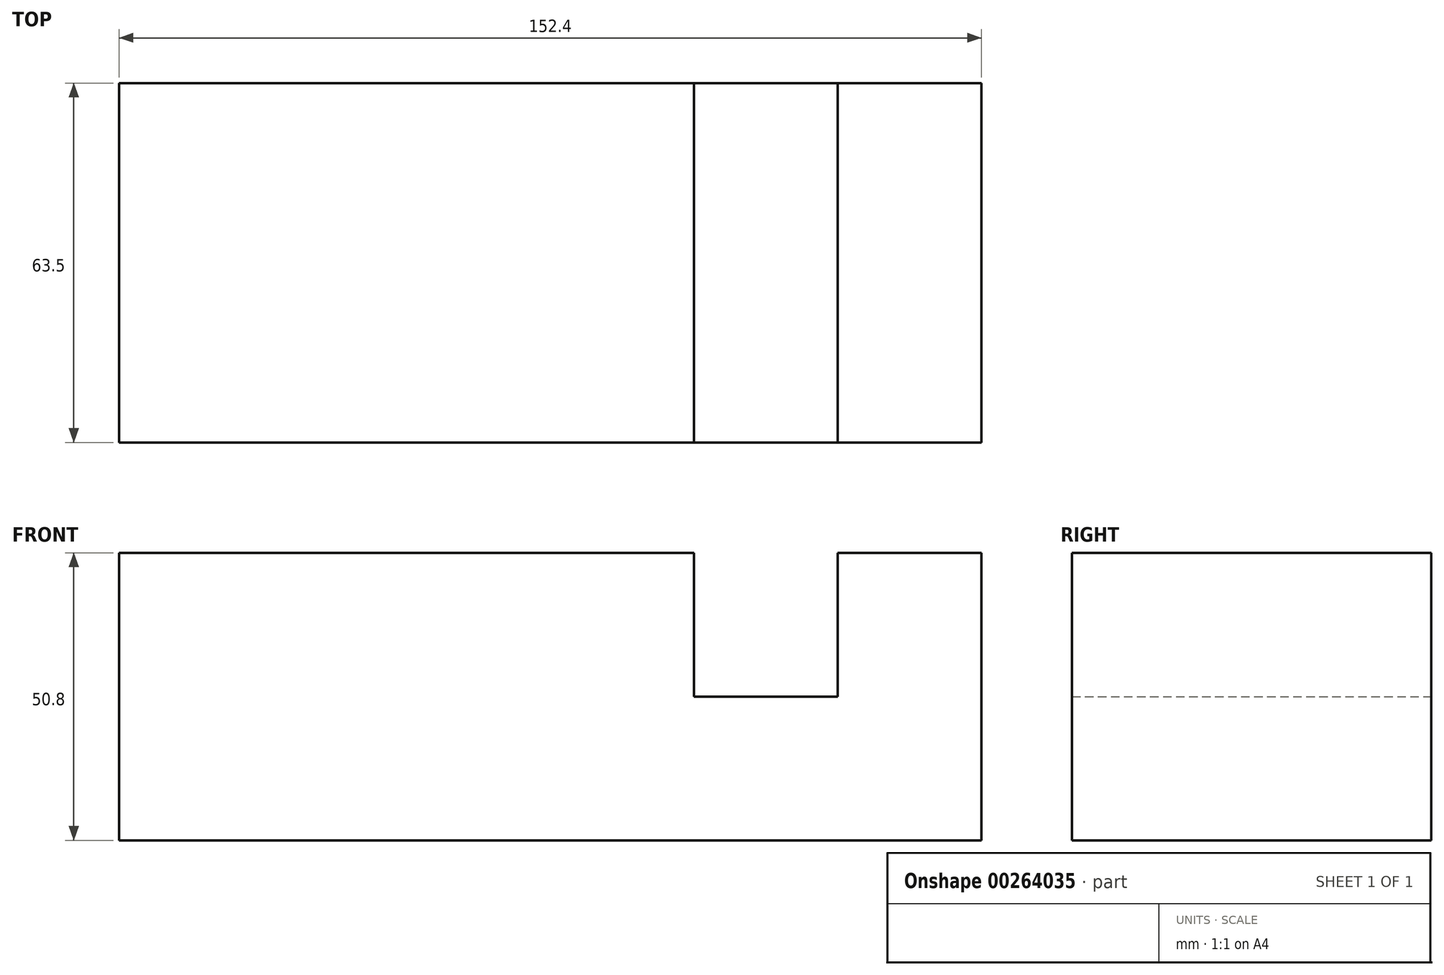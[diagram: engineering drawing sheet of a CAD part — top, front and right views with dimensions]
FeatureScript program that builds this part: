
annotation { "Feature Type Name" : "Feature", "Feature Type Description" : "" }
export const myFeature = defineFeature(function(context is Context, id is Id, definition is map)
    precondition{}
    {
        {
            var Q0;
            Q0=qCreatedBy(makeId("Front.planeOp"),FACE);
            var sketch = newSketch(context, id + "F0", { "sketchPlane" : qUnion([Q0])});
            skLineSegment(sketch, "E0", {"start": v(-75.34, -27.2) * mm, "end": v(77.06, -27.2) * mm});
            skLineSegment(sketch, "E1", {"start": v(77.06, -27.2) * mm, "end": v(77.06, 23.6) * mm});
            skLineSegment(sketch, "E2", {"start": v(77.06, 23.6) * mm, "end": v(51.66, 23.6) * mm});
            skLineSegment(sketch, "E3", {"start": v(51.66, 23.6) * mm, "end": v(51.66, -1.8) * mm});
            skLineSegment(sketch, "E4", {"start": v(51.66, -1.8) * mm, "end": v(26.26, -1.8) * mm});
            skLineSegment(sketch, "E5", {"start": v(26.26, -1.8) * mm, "end": v(26.26, 23.6) * mm});
            skLineSegment(sketch, "E6", {"start": v(26.26, 23.6) * mm, "end": v(-75.34, 23.6) * mm});
            skLineSegment(sketch, "E7", {"start": v(-75.34, 23.6) * mm, "end": v(-75.34, -27.2) * mm});
            skSolve(sketch);
        }
        {
            var Q0;
            Q0=makeQuery(id+"F0.imprint","IMPRINT",FACE,{"disambiguationData":[TD([[makeQuery(id+"F0.imprint","IMPRINT",EDGE,{"derivedFrom":sQuery(id+"F0.wireOp",EDGE,"E0")}),1.0]])]});
            extrude(context, id + "F1", {"entities" : qUnion([Q0]), "depth" : 38.1 * mm});
        }
        {
            var Q0;
            Q0=makeQuery(id+"F1.opExtrude","CAP_FACE",FACE,{"disambiguationData":[OSD([sQuery(id+"F0.wireOp",EDGE,"E0"),sQuery(id+"F0.wireOp",EDGE,"E1"),sQuery(id+"F0.wireOp",EDGE,"E2"),sQuery(id+"F0.wireOp",EDGE,"E3"),sQuery(id+"F0.wireOp",EDGE,"E4"),sQuery(id+"F0.wireOp",EDGE,"E5"),sQuery(id+"F0.wireOp",EDGE,"E6"),sQuery(id+"F0.wireOp",EDGE,"E7")])],"isStart":true});
            extrude(context, id + "F2", {"entities" : qUnion([Q0]), "operationType" : NewBodyOperationType.ADD, "depth" : 25.4 * mm});
        }
    });
